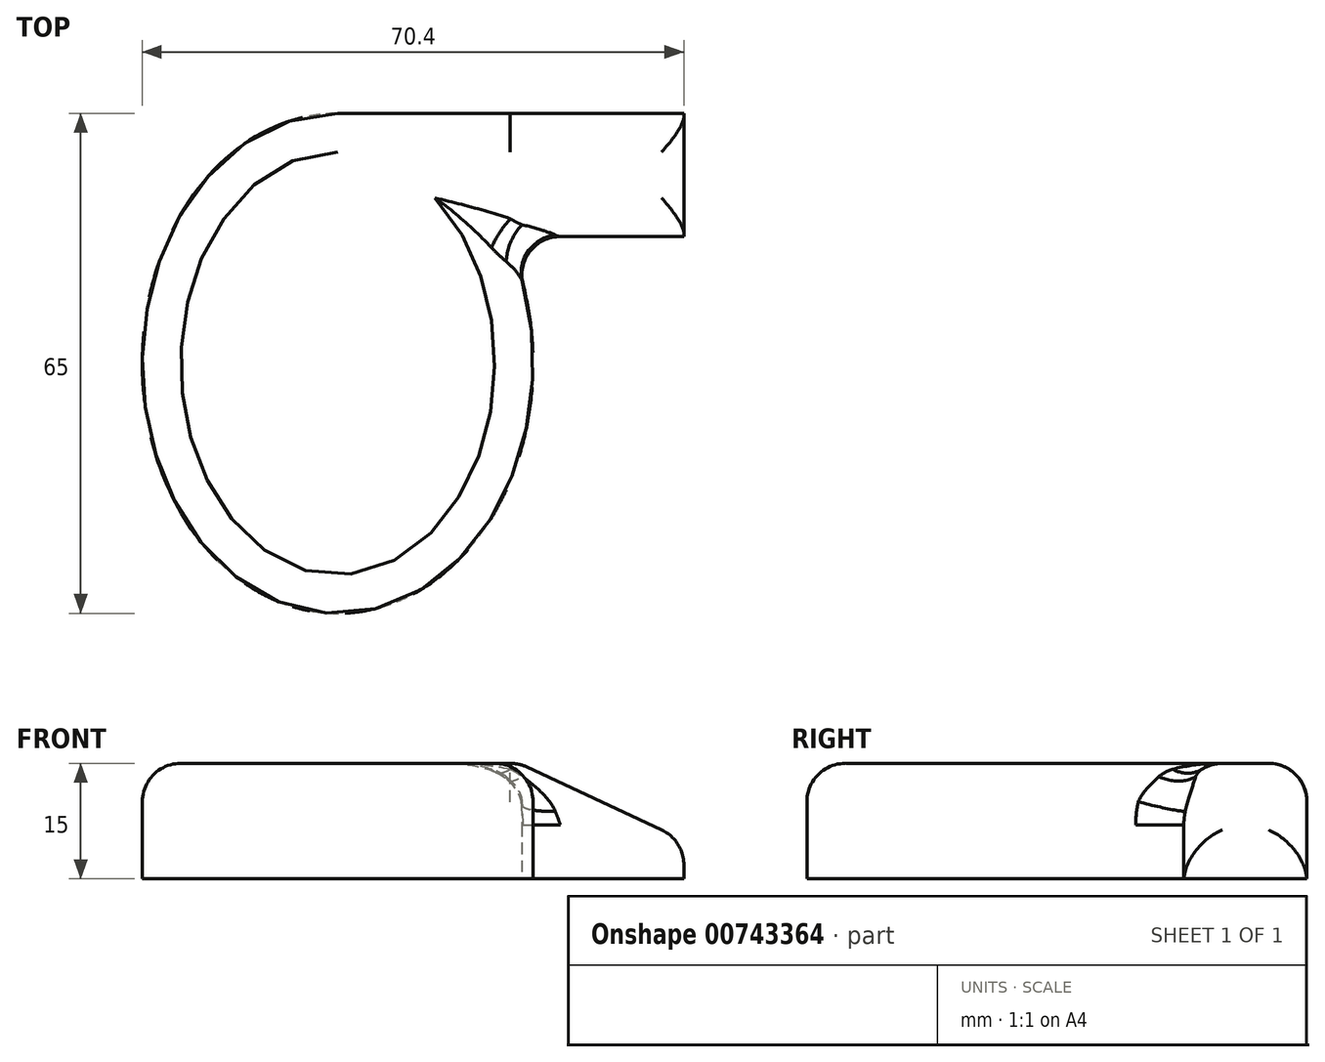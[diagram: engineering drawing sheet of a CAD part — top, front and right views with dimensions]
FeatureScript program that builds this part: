
annotation { "Feature Type Name" : "Feature", "Feature Type Description" : "" }
export const myFeature = defineFeature(function(context is Context, id is Id, definition is map)
    precondition{}
    {
        {
            var Q0;
            Q0=qCreatedBy(makeId("Top.planeOp"),FACE);
            var sketch = newSketch(context, id + "F0", { "sketchPlane" : qUnion([Q0])});
            skEllipse(sketch, "E0", {"center": v(0, 0) * mm, "majorRadius": 32.5 * mm, "minorRadius": 25.4 * mm, "majorAxis": v(0, 1)});
            skLineSegment(sketch, "E1", {"start": v(0, 32.5) * mm, "end": v(45, 32.5) * mm});
            skLineSegment(sketch, "E2", {"start": v(45, 32.5) * mm, "end": v(45, 16.5) * mm});
            skLineSegment(sketch, "E3", {"start": v(45, 16.5) * mm, "end": v(21.88, 16.5) * mm});
            skSolve(sketch);
        }
        {
            var Q0;
            {var subQ0=sQuery(id+"F0.wireOp",EDGE,"E0");var subQ1=makeQuery(id+"F0.imprint","INTERSECT",VERTEX,{"derivedFrom":[subQ0,sQuery(id+"F0.wireOp",EDGE,"E1")]});Q0=makeQuery(id+"F0.imprint","IMPRINT",FACE,{"disambiguationData":[TD([[makeQuery(id+"F0.imprint","IMPRINT",EDGE,{"disambiguationData":[TD([[subQ1,-1.0]])],"derivedFrom":subQ0}),1.0]])]});}
            var Q1;
            {var subQ0=sQuery(id+"F0.wireOp",EDGE,"E1");Q1=makeQuery(id+"F0.imprint","IMPRINT",FACE,{"disambiguationData":[TD([[makeQuery(id+"F0.imprint","IMPRINT",EDGE,{"derivedFrom":subQ0}),-1.0]])]});}
            extrude(context, id + "F1", {"entities" : qUnion([Q0, Q1]), "depth" : 15 * mm, "offsetDistance" : 25 * mm});
        }
        {
            var Q0;
            Q0=makeQuery(id+"F1.opExtrude","CAP_EDGE",EDGE,{"disambiguationData":[OSD([sQuery(id+"F0.wireOp",EDGE,"E2")])],"isStart":false});
            chamfer(context, id + "F2", {"entities" : qUnion([Q0]), "chamferType" : ChamferType.OFFSET_ANGLE, "width" : 10 * mm, "oppositeDirection" : false, "angle" : 65 * degree, "tangentPropagation" : true});
        }
        {
            var Q0;
            Q0=makeQuery(id+"F1.opExtrude","CAP_EDGE",EDGE,{"disambiguationData":[OSD([sQuery(id+"F0.wireOp",EDGE,"E0")])],"isStart":false});
            fillet(context, id + "F3", {"entities" : qUnion([Q0]), "radius" : 5 * mm, "tangentPropagation" : true, "allowEdgeOverflow" : false});
        }
        {
            var Q0;
            Q0=makeQuery(id+"F2.opChamfer","BLEND_EDGE",EDGE,{"blendedFrom":[makeQuery(id+"F1.opExtrude","CAP_EDGE",EDGE,{"disambiguationData":[OSD([sQuery(id+"F0.wireOp",EDGE,"E2")])],"isStart":false}),makeQuery(id+"F1.opExtrude","SWEPT_FACE",FACE,{"disambiguationData":[OSD([sQuery(id+"F0.wireOp",EDGE,"E3")])]})],"blendedInto":[makeQuery(id+"F1.opExtrude","SWEPT_FACE",FACE,{"disambiguationData":[OSD([sQuery(id+"F0.wireOp",EDGE,"E3")])]})]});
            var Q1;
            Q1=makeQuery(id+"F1.opExtrude","CAP_EDGE",EDGE,{"disambiguationData":[OSD([sQuery(id+"F0.wireOp",EDGE,"E3")])],"isStart":false});
            var Q2;
            {var subQ0=sQuery(id+"F0.wireOp",EDGE,"E2");Q2=makeQuery(id+"F2.opChamfer","BLEND_EDGE",EDGE,{"blendedFrom":[makeQuery(id+"F1.opExtrude","CAP_EDGE",EDGE,{"disambiguationData":[OSD([subQ0])],"isStart":false}),makeQuery(id+"F1.opExtrude","SWEPT_FACE",FACE,{"disambiguationData":[OSD([subQ0])]})],"blendedInto":[makeQuery(id+"F1.opExtrude","SWEPT_FACE",FACE,{"disambiguationData":[OSD([subQ0])]})]});}
            var Q3;
            Q3=makeQuery(id+"F2.opChamfer","BLEND_EDGE",EDGE,{"blendedFrom":[makeQuery(id+"F1.opExtrude","CAP_EDGE",EDGE,{"disambiguationData":[OSD([sQuery(id+"F0.wireOp",EDGE,"E2")])],"isStart":false}),makeQuery(id+"F1.opExtrude","SWEPT_FACE",FACE,{"disambiguationData":[OSD([sQuery(id+"F0.wireOp",EDGE,"E1")])]})],"blendedInto":[makeQuery(id+"F1.opExtrude","SWEPT_FACE",FACE,{"disambiguationData":[OSD([sQuery(id+"F0.wireOp",EDGE,"E1")])]})]});
            fillet(context, id + "F4", {"entities" : qUnion([Q0, Q1, Q2, Q3]), "radius" : 5 * mm, "tangentPropagation" : true, "allowEdgeOverflow" : false});
        }
        {
            var Q0;
            Q0=makeQuery(id+"F1.opExtrude","SWEPT_EDGE",EDGE,{"disambiguationData":[OSD([sQuery(id+"F0.wireOp",EDGE,"E0"),sQuery(id+"F0.wireOp",EDGE,"E3")])]});
            fillet(context, id + "F5", {"entities" : qUnion([Q0]), "radius" : 5 * mm, "tangentPropagation" : true, "allowEdgeOverflow" : false});
        }
    });
